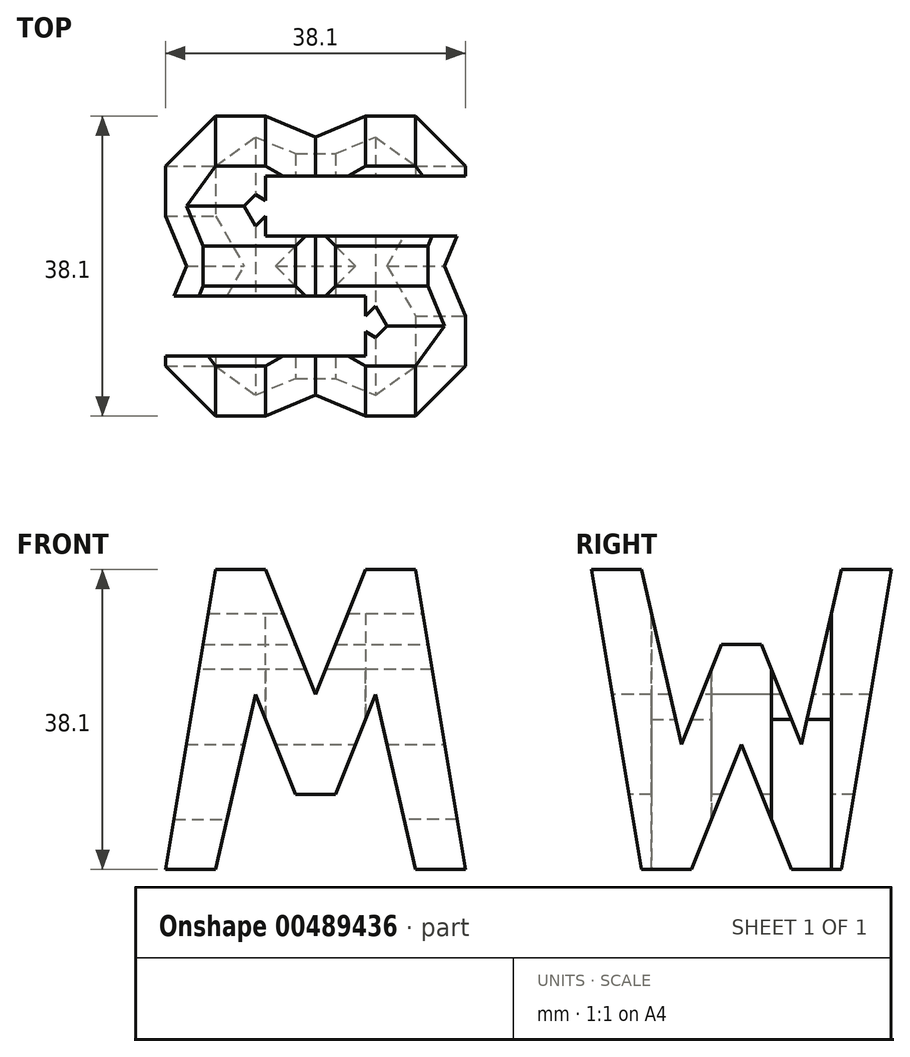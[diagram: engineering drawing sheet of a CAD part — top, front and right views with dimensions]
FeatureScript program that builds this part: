
annotation { "Feature Type Name" : "Feature", "Feature Type Description" : "" }
export const myFeature = defineFeature(function(context is Context, id is Id, definition is map)
    precondition{}
    {
        {
            var Q0;
            Q0=qCreatedBy(makeId("Front.planeOp"),FACE);
            var sketch = newSketch(context, id + "F0", { "sketchPlane" : qUnion([Q0])});
            skLineSegment(sketch, "E0", {"start": v(38.1, 38.1) * mm, "end": v(0, 38.1) * mm});
            skLineSegment(sketch, "E1", {"start": v(38.1, 38.1) * mm, "end": v(38.1, 0) * mm});
            skLineSegment(sketch, "E2", {"start": v(0, 0) * mm, "end": v(38.1, 0) * mm});
            skLineSegment(sketch, "E3", {"start": v(0, 38.1) * mm, "end": v(0, 0) * mm});
            skSolve(sketch);
        }
        {
            var Q0;
            Q0=makeQuery(id+"F0.imprint","IMPRINT",FACE,{"disambiguationData":[TD([[makeQuery(id+"F0.imprint","IMPRINT",EDGE,{"derivedFrom":sQuery(id+"F0.wireOp",EDGE,"E0")}),1.0]])]});
            extrude(context, id + "F1", {"entities" : qUnion([Q0]), "oppositeDirection" : true, "depth" : 38.1 * mm, "offsetDistance" : 25.4 * mm});
        }
        {
            var Q0;
            Q0=qCreatedBy(makeId("Front.planeOp"),FACE);
            cPlane(context, id + "F2", {"entities" : qUnion([Q0]), "cplaneType" : CPlaneType.OFFSET, "offset" : 38.1 * mm, "width" : 152.4 * mm, "height" : 152.4 * mm});
        }
        {
            var Q0;
            Q0=qCreatedBy(makeId("Right.planeOp"),FACE);
            cPlane(context, id + "F3", {"entities" : qUnion([Q0]), "cplaneType" : CPlaneType.OFFSET, "offset" : 38.1 * mm, "width" : 152.4 * mm, "height" : 152.4 * mm});
        }
        {
            var Q0;
            Q0=qCreatedBy(makeId("Top.planeOp"),FACE);
            cPlane(context, id + "F4", {"entities" : qUnion([Q0]), "cplaneType" : CPlaneType.OFFSET, "offset" : 38.1 * mm, "width" : 152.4 * mm, "height" : 152.4 * mm});
        }
        {
            var Q0;
            Q0=qCreatedBy(id+"F3.planeOp",FACE);
            var sketch = newSketch(context, id + "F5", { "sketchPlane" : qUnion([Q0])});
            skLineSegment(sketch, "E4", {"start": v(0, 0) * mm, "end": v(0, 38.1) * mm});
            skLineSegment(sketch, "E5", {"start": v(0, 0) * mm, "end": v(38.1, 0) * mm});
            skLineSegment(sketch, "E6", {"start": v(38.1, 0) * mm, "end": v(38.1, 38.1) * mm});
            skLineSegment(sketch, "E7", {"start": v(38.1, 38.1) * mm, "end": v(0, 38.1) * mm});
            skLineSegment(sketch, "E8", {"start": v(0, 38.1) * mm, "end": v(6.35, 0) * mm});
            skLineSegment(sketch, "E9", {"start": v(6.35, 38.1) * mm, "end": v(11.43, 15.88) * mm});
            skLineSegment(sketch, "E10", {"start": v(11.43, 15.88) * mm, "end": v(16.51, 28.58) * mm});
            skLineSegment(sketch, "E11", {"start": v(16.51, 28.58) * mm, "end": v(21.6, 28.58) * mm});
            skLineSegment(sketch, "E12", {"start": v(21.6, 28.58) * mm, "end": v(26.67, 15.88) * mm});
            skLineSegment(sketch, "E13", {"start": v(26.67, 15.87) * mm, "end": v(31.75, 38.1) * mm});
            skLineSegment(sketch, "E14", {"start": v(38.1, 38.1) * mm, "end": v(31.75, 0) * mm});
            skLineSegment(sketch, "E15", {"start": v(19.05, 15.88) * mm, "end": v(12.7, 0) * mm});
            skLineSegment(sketch, "E16", {"start": v(19.05, 15.88) * mm, "end": v(25.4, 0) * mm});
            skSolve(sketch);
        }
        {
            var Q0;
            {var subQ0=sQuery(id+"F5.wireOp",EDGE,"E9");Q0=makeQuery(id+"F5.imprint","IMPRINT",FACE,{"disambiguationData":[TD([[makeQuery(id+"F5.imprint","IMPRINT",EDGE,{"derivedFrom":subQ0}),1.0]])]});}
            var Q1;
            {var subQ0=sQuery(id+"F5.wireOp",EDGE,"E4");Q1=makeQuery(id+"F5.imprint","IMPRINT",FACE,{"disambiguationData":[TD([[makeQuery(id+"F5.imprint","IMPRINT",EDGE,{"derivedFrom":subQ0}),-1.0]])]});}
            var Q2;
            {var subQ0=sQuery(id+"F5.wireOp",EDGE,"E15");Q2=makeQuery(id+"F5.imprint","IMPRINT",FACE,{"disambiguationData":[TD([[makeQuery(id+"F5.imprint","IMPRINT",EDGE,{"derivedFrom":subQ0}),1.0]])]});}
            var Q3;
            {var subQ0=sQuery(id+"F5.wireOp",EDGE,"E6");Q3=makeQuery(id+"F5.imprint","IMPRINT",FACE,{"disambiguationData":[TD([[makeQuery(id+"F5.imprint","IMPRINT",EDGE,{"derivedFrom":subQ0}),1.0]])]});}
            extrude(context, id + "F6", {"entities" : qUnion([Q0, Q1, Q2, Q3]), "operationType" : NewBodyOperationType.REMOVE, "oppositeDirection" : true, "depth" : 38.1 * mm, "offsetDistance" : 25.4 * mm});
        }
        {
            var Q0;
            Q0=qCreatedBy(id+"F2.planeOp",FACE);
            var sketch = newSketch(context, id + "F7", { "sketchPlane" : qUnion([Q0])});
            skLineSegment(sketch, "E17", {"start": v(38.1, 38.1) * mm, "end": v(38.1, 0) * mm});
            skLineSegment(sketch, "E18", {"start": v(38.1, 0) * mm, "end": v(0, 0) * mm});
            skLineSegment(sketch, "E19", {"start": v(0, 0) * mm, "end": v(0, 38.1) * mm});
            skLineSegment(sketch, "E20", {"start": v(0, 38.1) * mm, "end": v(38.1, 38.1) * mm});
            skLineSegment(sketch, "E21", {"start": v(6.35, 38.1) * mm, "end": v(0, 0) * mm});
            skLineSegment(sketch, "E22", {"start": v(6.35, 0) * mm, "end": v(11.43, 22.23) * mm});
            skLineSegment(sketch, "E23", {"start": v(11.43, 22.23) * mm, "end": v(16.51, 9.53) * mm});
            skLineSegment(sketch, "E24", {"start": v(16.51, 9.53) * mm, "end": v(21.6, 9.53) * mm});
            skLineSegment(sketch, "E25", {"start": v(21.6, 9.53) * mm, "end": v(26.67, 22.23) * mm});
            skLineSegment(sketch, "E26", {"start": v(26.67, 22.23) * mm, "end": v(31.75, 0) * mm});
            skLineSegment(sketch, "E27", {"start": v(38.1, 0) * mm, "end": v(31.75, 38.1) * mm});
            skLineSegment(sketch, "E28", {"start": v(31.75, 38.1) * mm, "end": v(25.4, 38.1) * mm});
            skLineSegment(sketch, "E29", {"start": v(25.4, 38.1) * mm, "end": v(19.05, 22.23) * mm});
            skLineSegment(sketch, "E30", {"start": v(19.05, 22.23) * mm, "end": v(12.7, 38.1) * mm});
            skLineSegment(sketch, "E31", {"start": v(12.7, 38.1) * mm, "end": v(6.35, 38.1) * mm});
            skSolve(sketch);
        }
        {
            var Q0;
            {var subQ0=sQuery(id+"F7.wireOp",EDGE,"E19");Q0=makeQuery(id+"F7.imprint","IMPRINT",FACE,{"disambiguationData":[TD([[makeQuery(id+"F7.imprint","IMPRINT",EDGE,{"derivedFrom":subQ0}),-1.0]])]});}
            var Q1;
            {var subQ0=sQuery(id+"F7.wireOp",EDGE,"E29");Q1=makeQuery(id+"F7.imprint","IMPRINT",FACE,{"disambiguationData":[TD([[makeQuery(id+"F7.imprint","IMPRINT",EDGE,{"derivedFrom":subQ0}),-1.0]])]});}
            var Q2;
            {var subQ0=sQuery(id+"F7.wireOp",EDGE,"E17");Q2=makeQuery(id+"F7.imprint","IMPRINT",FACE,{"disambiguationData":[TD([[makeQuery(id+"F7.imprint","IMPRINT",EDGE,{"derivedFrom":subQ0}),-1.0]])]});}
            var Q3;
            {var subQ0=sQuery(id+"F7.wireOp",EDGE,"E22");Q3=makeQuery(id+"F7.imprint","IMPRINT",FACE,{"disambiguationData":[TD([[makeQuery(id+"F7.imprint","IMPRINT",EDGE,{"derivedFrom":subQ0}),-1.0]])]});}
            extrude(context, id + "F8", {"entities" : qUnion([Q0, Q1, Q2, Q3]), "operationType" : NewBodyOperationType.REMOVE, "oppositeDirection" : true, "depth" : 76.2 * mm, "offsetDistance" : 25.4 * mm});
        }
        {
            var Q0;
            Q0=qCreatedBy(id+"F4.planeOp",FACE);
            var sketch = newSketch(context, id + "F9", { "sketchPlane" : qUnion([Q0])});
            skLineSegment(sketch, "E32.bottom", {"start": v(0, 0) * mm, "end": v(38.1, 0) * mm});
            skLineSegment(sketch, "E32.top", {"start": v(0, 38.1) * mm, "end": v(38.1, 38.1) * mm});
            skLineSegment(sketch, "E32.left", {"start": v(0, 0) * mm, "end": v(0, 38.1) * mm});
            skLineSegment(sketch, "E32.right", {"start": v(38.1, 0) * mm, "end": v(38.1, 38.1) * mm});
            skLineSegment(sketch, "E33.bottom", {"start": v(38.1, 38.1) * mm, "end": v(38.1, 38.1) * mm});
            skLineSegment(sketch, "E33.top", {"start": v(38.1, 38.1) * mm, "end": v(38.1, 38.1) * mm});
            skLineSegment(sketch, "E33.left", {"start": v(38.1, 38.1) * mm, "end": v(38.1, 38.1) * mm});
            skLineSegment(sketch, "E33.right", {"start": v(38.1, 38.1) * mm, "end": v(38.1, 38.1) * mm});
            skLineSegment(sketch, "E34", {"start": v(38.1, 30.48) * mm, "end": v(38.1, 32.12) * mm});
            skLineSegment(sketch, "E35", {"start": v(0, 38.1) * mm, "end": v(0, 0) * mm});
            skLineSegment(sketch, "E36", {"start": v(38.1, 30.48) * mm, "end": v(12.7, 30.48) * mm});
            skLineSegment(sketch, "E37", {"start": v(12.7, 30.48) * mm, "end": v(12.7, 22.86) * mm});
            skLineSegment(sketch, "E38", {"start": v(12.7, 22.86) * mm, "end": v(38.1, 22.86) * mm});
            skLineSegment(sketch, "E39", {"start": v(0, 15.24) * mm, "end": v(25.4, 15.24) * mm});
            skLineSegment(sketch, "E40", {"start": v(25.4, 15.24) * mm, "end": v(25.4, 7.62) * mm});
            skLineSegment(sketch, "E41", {"start": v(25.4, 7.62) * mm, "end": v(0, 7.62) * mm});
            skSolve(sketch);
        }
        {
            var Q0;
            {var subQ0=sQuery(id+"F9.wireOp",EDGE,"E36");Q0=makeQuery(id+"F9.imprint","IMPRINT",FACE,{"disambiguationData":[TD([[makeQuery(id+"F9.imprint","IMPRINT",EDGE,{"derivedFrom":subQ0}),1.0]])]});}
            var Q1;
            {var subQ0=sQuery(id+"F9.wireOp",EDGE,"E39");Q1=makeQuery(id+"F9.imprint","IMPRINT",FACE,{"disambiguationData":[TD([[makeQuery(id+"F9.imprint","IMPRINT",EDGE,{"derivedFrom":subQ0}),-1.0]])]});}
            extrude(context, id + "F10", {"entities" : qUnion([Q0, Q1]), "operationType" : NewBodyOperationType.REMOVE, "oppositeDirection" : true, "depth" : 38.1 * mm, "offsetDistance" : 25.4 * mm});
        }
    });
